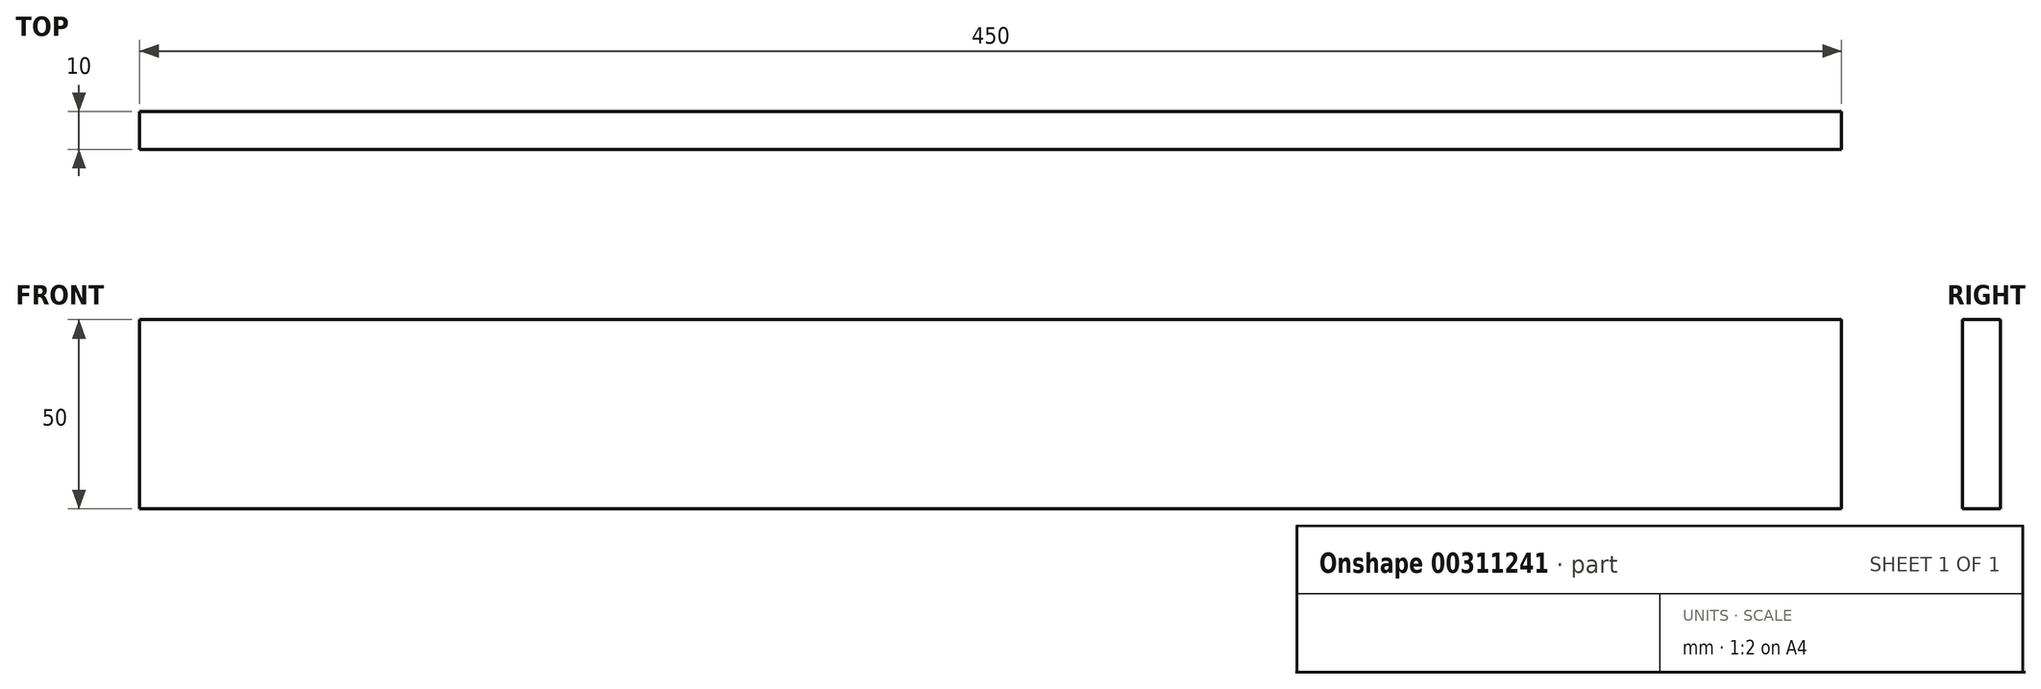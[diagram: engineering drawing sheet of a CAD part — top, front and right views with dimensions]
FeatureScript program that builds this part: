
annotation { "Feature Type Name" : "Feature", "Feature Type Description" : "" }
export const myFeature = defineFeature(function(context is Context, id is Id, definition is map)
    precondition{}
    {
        {
            var Q0;
            Q0=qCreatedBy(makeId("Front.planeOp"),FACE);
            var sketch = newSketch(context, id + "F0", { "sketchPlane" : qUnion([Q0])});
            skLineSegment(sketch, "E0.bottom", {"start": v(0, 0) * mm, "end": v(-450, 0) * mm});
            skLineSegment(sketch, "E0.top", {"start": v(0, 50) * mm, "end": v(-450, 50) * mm});
            skLineSegment(sketch, "E0.left", {"start": v(0, 0) * mm, "end": v(0, 50) * mm});
            skLineSegment(sketch, "E0.right", {"start": v(-450, 0) * mm, "end": v(-450, 50) * mm});
            skSolve(sketch);
        }
        {
            var Q0;
            Q0=makeQuery(id+"F0.imprint","IMPRINT",FACE,{"disambiguationData":[TD([[makeQuery(id+"F0.imprint","IMPRINT",EDGE,{"derivedFrom":sQuery(id+"F0.wireOp",EDGE,"E0.bottom")}),-1.0]])]});
            extrude(context, id + "F1", {"entities" : qUnion([Q0]), "depth" : 10 * mm});
        }
    });
